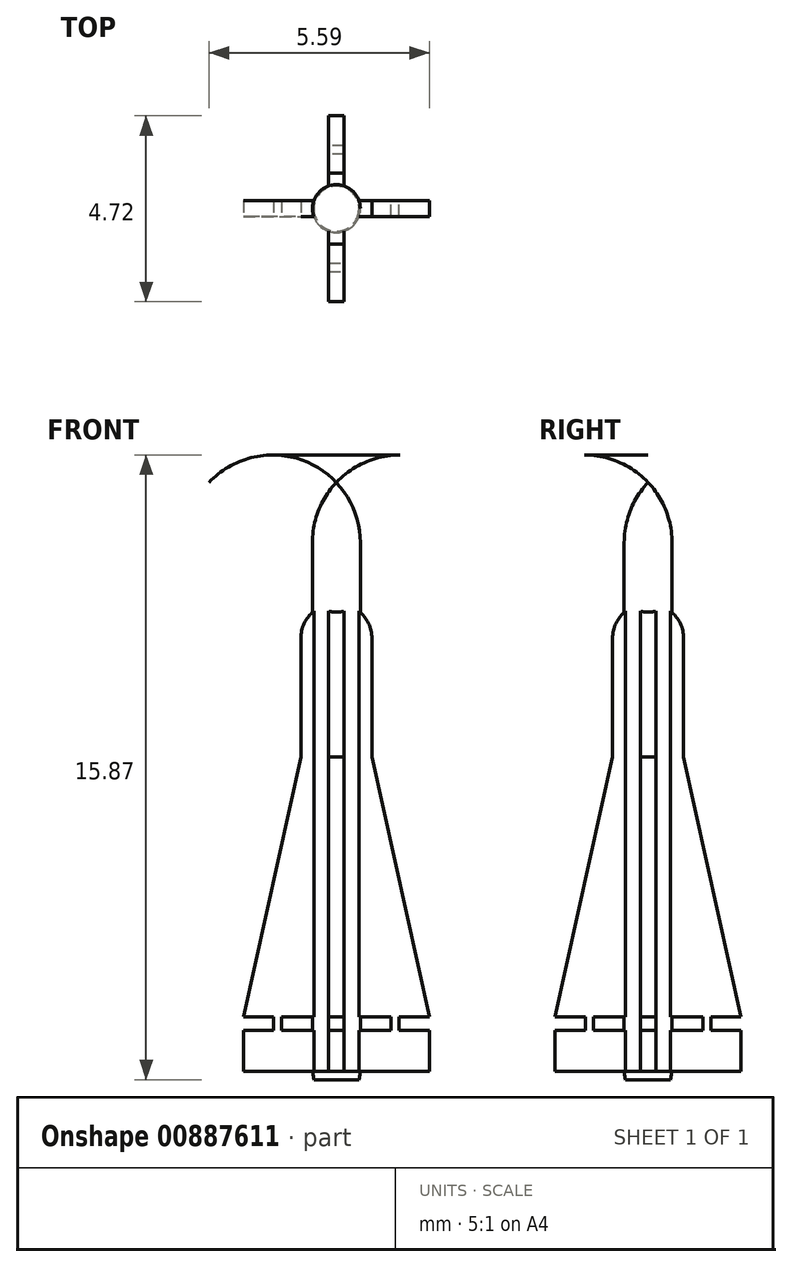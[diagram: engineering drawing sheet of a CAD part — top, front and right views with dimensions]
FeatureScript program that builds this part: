
annotation { "Feature Type Name" : "Feature", "Feature Type Description" : "" }
export const myFeature = defineFeature(function(context is Context, id is Id, definition is map)
    precondition{}
    {
        {
            var Q0;
            Q0=qCreatedBy(makeId("Front.planeOp"),FACE);
            var sketch = newSketch(context, id + "F0", { "sketchPlane" : qUnion([Q0])});
            skLineSegment(sketch, "E0", {"start": v(0, 0) * mm, "end": v(0, 15.17) * mm});
            skLineSegment(sketch, "E1", {"start": v(0.6, 13.65) * mm, "end": v(0.6, 0) * mm});
            skLineSegment(sketch, "E2", {"start": v(0.6, 0) * mm, "end": v(0, 0) * mm});
            skLineSegment(sketch, "E3", {"start": v(0.6, 0.2) * mm, "end": v(0.57, 0) * mm});
            skArc(sketch, "E4", {"start": v(0.6, 13.65) * mm, "mid": v(0.45, 14.47) * mm, "end": v(0, 15.17) * mm});
            skSolve(sketch);
        }
        {
            var Q0;
            {var subQ0=sQuery(id+"F0.wireOp",EDGE,"mrwio9nY-PsAZ-Zbfy-NhIU-sYq0QVbgGXAG");Q0=makeQuery(id+"F0.imprint","IMPRINT",FACE,{"disambiguationData":[TD([[makeQuery(id+"F0.imprint","IMPRINT",EDGE,{"derivedFrom":subQ0}),-1.0]])]});}
            var Q1;
            {var subQ7=sQuery(id+"F0.wireOp",EDGE,"E0");Q1=makeQuery(id+"F0.imprint","IMPRINT",FACE,{"disambiguationData":[TD([[makeQuery(id+"F0.imprint","IMPRINT",EDGE,{"derivedFrom":subQ7}),-1.0]])]});}
            var Q2;
            Q2=sQuery(id+"F0.wireOp",EDGE,"E0");
            revolve(context, id + "F1", {"surfaceOperationType" : NewSurfaceOperationType.NEW, "entities" : qUnion([Q0, Q1]), "axis" : qUnion([Q2]), "revolveType" : RevolveType.FULL});
        }
        {
            var Q0;
            Q0=qCreatedBy(makeId("Front.planeOp"),FACE);
            var sketch = newSketch(context, id + "F2", { "sketchPlane" : qUnion([Q0])});
            skLineSegment(sketch, "E5", {"start": v(0, 0) * mm, "end": v(0, 12.11) * mm});
            skLineSegment(sketch, "E6", {"start": v(0.4, 1.6) * mm, "end": v(0.4, 1.25) * mm});
            skLineSegment(sketch, "E7", {"start": v(0.4, 1.25) * mm, "end": v(2.36, 1.25) * mm});
            skLineSegment(sketch, "E8", {"start": v(0.6, 0) * mm, "end": v(0.6, 32.87) * mm, "construction": true});
            skLineSegment(sketch, "E9", {"start": v(0.4, 1.6) * mm, "end": v(2.36, 1.6) * mm});
            skLineSegment(sketch, "E10", {"start": v(2.36, 1.6) * mm, "end": v(0.9, 8.2) * mm});
            skPoint(sketch, "E11", {"position": v(0.6, 1.6) * mm});
            skLineSegment(sketch, "E12", {"start": v(0, 0.2) * mm, "end": v(2.36, 0.2) * mm});
            skLineSegment(sketch, "E13", {"start": v(2.36, 0.2) * mm, "end": v(2.36, 1.25) * mm});
            skLineSegment(sketch, "E14", {"start": v(1.39, 1.6) * mm, "end": v(1.39, 1.25) * mm});
            skLineSegment(sketch, "E15", {"start": v(1.6, 1.6) * mm, "end": v(1.6, 1.25) * mm});
            skLineSegment(sketch, "E16.0", {"start": v(0.6, 0.2) * mm, "end": v(-0.6, 0.2) * mm});
            skLineSegment(sketch, "E17", {"start": v(0.9, 8.2) * mm, "end": v(0.9, 11.2) * mm});
            skArc(sketch, "E18", {"start": v(0.9, 11.2) * mm, "mid": v(0.64, 11.85) * mm, "end": v(0, 12.11) * mm});
            skPoint(sketch, "E19", {"position": v(0.6, 11.88) * mm});
            skPoint(sketch, "E20", {"position": v(3.15, 11.37) * mm});
            skSolve(sketch);
        }
        {
            var Q0;
            {var subQ3=sQuery(id+"F2.wireOp",EDGE,"E14");var subQ14=sQuery(id+"F2.wireOp",EDGE,"E6");Q0=qUnion([makeQuery(id+"F2.imprint","IMPRINT",FACE,{"disambiguationData":[TD([[makeQuery(id+"F2.imprint","IMPRINT",EDGE,{"derivedFrom":subQ14}),-1.0]])]}),makeQuery(id+"F2.imprint","IMPRINT",FACE,{"disambiguationData":[TD([[makeQuery(id+"F2.imprint","IMPRINT",EDGE,{"derivedFrom":subQ3}),1.0]])]})]);}
            extrude(context, id + "F3", {"entities" : qUnion([Q0]), "operationType" : NewBodyOperationType.ADD, "depth" : .4 * mm, "offsetDistance" : 25 * mm, "symmetric" : true});
        }
        {
            var Q0;
            Q0=makeQuery(id+"F1.opRevolve","SWEPT_BODY",BODY,{"disambiguationData":[OSD([sQuery(id+"F0.wireOp",EDGE,"E0"),sQuery(id+"F0.wireOp",EDGE,"E1"),sQuery(id+"F0.wireOp",EDGE,"E2"),sQuery(id+"F0.wireOp",EDGE,"2EiOItwe-9FNA-eY8p-DkXH-AMy5AHyUmzZA"),sQuery(id+"F0.wireOp",EDGE,"lF35QjYl-MEgV-fRWE-0Yr6-Bt5vS8A7brRf")])]});
            var Q1;
            Q1=makeQuery(id+"F1.opRevolve","SWEPT_FACE",FACE,{"disambiguationData":[OSD([sQuery(id+"F0.wireOp",EDGE,"E1")])]});
            circularPattern(context, id + "F4", {"operationType" : NewBodyOperationType.ADD, "entities" : qUnion([Q0]), "axis" : qUnion([Q1]), "angle" : 360 * degree, "instanceCount" : 4, "equalSpace" : true, "computeTransformsWithoutBuiltin" : true});
        }
    });
